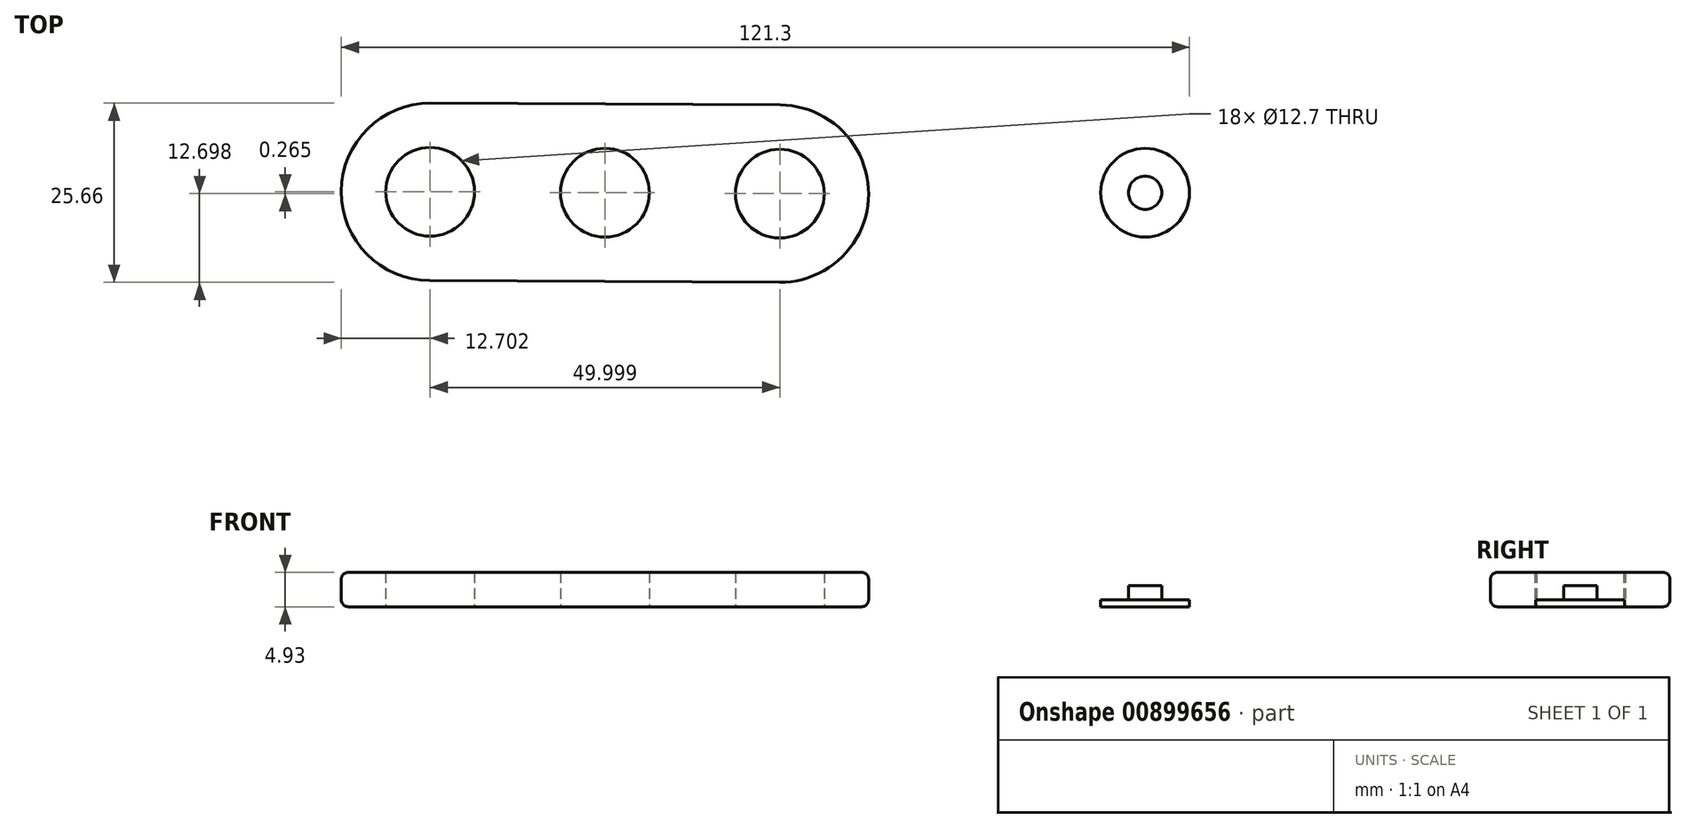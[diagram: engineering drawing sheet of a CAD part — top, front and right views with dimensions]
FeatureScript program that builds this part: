
annotation { "Feature Type Name" : "Feature", "Feature Type Description" : "" }
export const myFeature = defineFeature(function(context is Context, id is Id, definition is map)
    precondition{}
    {
        {
            var Q0;
            Q0=qCreatedBy(makeId("Top.planeOp"),FACE);
            var sketch = newSketch(context, id + "F0", { "sketchPlane" : qUnion([Q0])});
            skCircle(sketch, "E0", {"center": v(0, 0) * mm, "radius": 2.38 * mm});
            skCircle(sketch, "E1", {"center": v(0, 0) * mm, "radius": 6.35 * mm});
            skLineSegment(sketch, "E2.left", {"start": v(-102.18, 12.83) * mm, "end": v(-52.18, 12.57) * mm});
            skLineSegment(sketch, "E2.right", {"start": v(-102.32, -12.57) * mm, "end": v(-52.32, -12.83) * mm});
            skPoint(sketch, "E2.middle", {"position": v(-77.25, 0) * mm});
            skArc(sketch, "E3", {"start": v(-102.18, 12.83) * mm, "mid": v(-114.95, 0.2) * mm, "end": v(-102.32, -12.57) * mm});
            skArc(sketch, "E4", {"start": v(-52.32, -12.83) * mm, "mid": v(-39.55, -0.2) * mm, "end": v(-52.18, 12.57) * mm});
            skCircle(sketch, "E5", {"center": v(-102.25, 0.13) * mm, "radius": 6.35 * mm});
            skCircle(sketch, "E6", {"center": v(-52.25, -0.13) * mm, "radius": 6.35 * mm});
            skCircle(sketch, "E7", {"center": v(-77.25, 0) * mm, "radius": 6.35 * mm});
            skSolve(sketch);
        }
        {
            var Q0;
            Q0=makeQuery(id+"F0.imprint","IMPRINT",FACE,{"disambiguationData":[TD([[makeQuery(id+"F0.imprint","IMPRINT",EDGE,{"derivedFrom":sQuery(id+"F0.wireOp",EDGE,"E2.left")}),-1.0]])]});
            extrude(context, id + "F1", {"entities" : qUnion([Q0]), "depth" : 4.93 * mm, "offsetDistance" : 25 * mm});
        }
        {
            var Q0;
            Q0=makeQuery(id+"F1.opExtrude","CAP_EDGE",EDGE,{"disambiguationData":[OSD([sQuery(id+"F0.wireOp",EDGE,"E2.right")])],"isStart":false});
            var Q1;
            Q1=makeQuery(id+"F1.opExtrude","CAP_EDGE",EDGE,{"disambiguationData":[OSD([sQuery(id+"F0.wireOp",EDGE,"E2.right")])],"isStart":true});
            var Q2;
            Q2=makeQuery(id+"F1.opExtrude","CAP_EDGE",EDGE,{"disambiguationData":[OSD([sQuery(id+"F0.wireOp",EDGE,"E2.left")])],"isStart":true});
            fillet(context, id + "F2", {"entities" : qUnion([Q0, Q1, Q2]), "radius" : 1 * mm, "tangentPropagation" : true, "allowEdgeOverflow" : false});
        }
        {
            var Q0;
            Q0=makeQuery(id+"F0.imprint","IMPRINT",FACE,{"disambiguationData":[TD([[makeQuery(id+"F0.imprint","IMPRINT",EDGE,{"derivedFrom":sQuery(id+"F0.wireOp",EDGE,"E0")}),-1.0]])]});
            extrude(context, id + "F3", {"entities" : qUnion([Q0]), "depth" : 1 * mm, "offsetDistance" : 25 * mm});
        }
        {
            var Q0;
            Q0=makeQuery(id+"F0.imprint","IMPRINT",FACE,{"disambiguationData":[TD([[makeQuery(id+"F0.imprint","IMPRINT",EDGE,{"derivedFrom":sQuery(id+"F0.wireOp",EDGE,"E0")}),1.0]])]});
            extrude(context, id + "F4", {"entities" : qUnion([Q0]), "operationType" : NewBodyOperationType.ADD, "depth" : 3 * mm, "offsetDistance" : 25 * mm});
        }
    });
